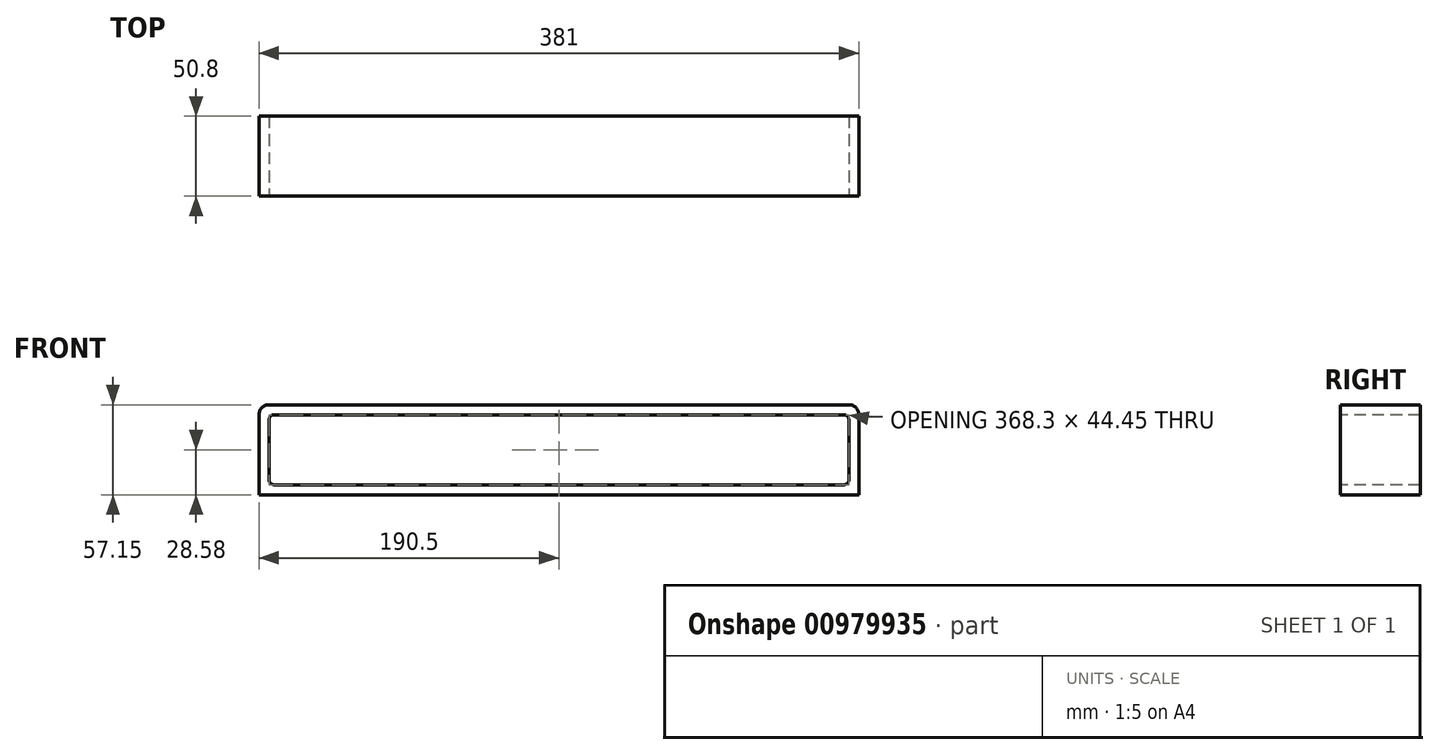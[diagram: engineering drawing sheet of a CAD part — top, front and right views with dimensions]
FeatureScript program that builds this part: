
annotation { "Feature Type Name" : "Feature", "Feature Type Description" : "" }
export const myFeature = defineFeature(function(context is Context, id is Id, definition is map)
    precondition{}
    {
        {
            var Q0;
            Q0=qCreatedBy(makeId("Front.planeOp"),FACE);
            var sketch = newSketch(context, id + "F0", { "sketchPlane" : qUnion([Q0])});
            skLineSegment(sketch, "E0.bottom", {"start": v(190.5, -28.57) * mm, "end": v(-190.5, -28.58) * mm});
            skLineSegment(sketch, "E0.top", {"start": v(190.5, 28.58) * mm, "end": v(-190.5, 28.57) * mm});
            skLineSegment(sketch, "E0.left", {"start": v(190.5, -28.57) * mm, "end": v(190.5, 28.58) * mm});
            skLineSegment(sketch, "E0.right", {"start": v(-190.5, -28.58) * mm, "end": v(-190.5, 28.57) * mm});
            skPoint(sketch, "E0.middle", {"position": v(0, 0) * mm});
            skSolve(sketch);
        }
        {
            var Q0;
            Q0=makeQuery(id+"F0.imprint","IMPRINT",FACE,{"disambiguationData":[TD([[makeQuery(id+"F0.imprint","IMPRINT",EDGE,{"derivedFrom":sQuery(id+"F0.wireOp",EDGE,"E0.bottom")}),-1.0]])]});
            extrude(context, id + "F1", {"entities" : qUnion([Q0]), "depth" : 50.8 * mm, "offsetDistance" : 25.4 * mm});
        }
        {
            var Q0;
            Q0=makeQuery(id+"F1.opExtrude","SWEPT_BODY",BODY,{"disambiguationData":[OSD([sQuery(id+"F0.wireOp",EDGE,"E0.bottom"),sQuery(id+"F0.wireOp",EDGE,"E0.top"),sQuery(id+"F0.wireOp",EDGE,"E0.left"),sQuery(id+"F0.wireOp",EDGE,"E0.right")])]});
            transform(context, id + "F2", {"entities" : qUnion([Q0]), "transformType" : TransformType.TRANSLATION_3D, "dx" : 0 * mm, "dy" : 50.8 * mm, "dz" : 0 * mm, "makeCopy" : false});
        }
        {
            var Q0;
            Q0=qCreatedBy(makeId("Front.planeOp"),FACE);
            var sketch = newSketch(context, id + "F3", { "sketchPlane" : qUnion([Q0])});
            skLineSegment(sketch, "E1.bottom", {"start": v(184.15, -22.22) * mm, "end": v(-184.15, -22.23) * mm});
            skLineSegment(sketch, "E1.top", {"start": v(184.15, 22.23) * mm, "end": v(-184.15, 22.22) * mm});
            skLineSegment(sketch, "E1.left", {"start": v(184.15, -22.22) * mm, "end": v(184.15, 22.23) * mm});
            skLineSegment(sketch, "E1.right", {"start": v(-184.15, -22.23) * mm, "end": v(-184.15, 22.22) * mm});
            skPoint(sketch, "E1.middle", {"position": v(0, 0) * mm});
            skSolve(sketch);
        }
        {
            var Q0;
            Q0=makeQuery(id+"F3.imprint","IMPRINT",FACE,{"disambiguationData":[TD([[makeQuery(id+"F3.imprint","IMPRINT",EDGE,{"derivedFrom":sQuery(id+"F3.wireOp",EDGE,"E1.bottom")}),-1.0]])]});
            extrude(context, id + "F4", {"entities" : qUnion([Q0]), "operationType" : NewBodyOperationType.REMOVE, "oppositeDirection" : true, "depth" : 50.8 * mm, "offsetDistance" : 25.4 * mm});
        }
        {
            var Q0;
            Q0=makeQuery(id+"F4.boolean.opBoolean","COPY",EDGE,{"derivedFrom":makeQuery(id+"F4.opExtrude","SWEPT_EDGE",EDGE,{"disambiguationData":[OSD([sQuery(id+"F3.wireOp",EDGE,"E1.bottom"),sQuery(id+"F3.wireOp",EDGE,"E1.left")])]})});
            var Q1;
            Q1=makeQuery(id+"F4.boolean.opBoolean","COPY",EDGE,{"derivedFrom":makeQuery(id+"F4.opExtrude","SWEPT_EDGE",EDGE,{"disambiguationData":[OSD([sQuery(id+"F3.wireOp",EDGE,"E1.top"),sQuery(id+"F3.wireOp",EDGE,"E1.left")])]})});
            var Q2;
            Q2=makeQuery(id+"F4.boolean.opBoolean","COPY",EDGE,{"derivedFrom":makeQuery(id+"F4.opExtrude","SWEPT_EDGE",EDGE,{"disambiguationData":[OSD([sQuery(id+"F3.wireOp",EDGE,"E1.top"),sQuery(id+"F3.wireOp",EDGE,"E1.right")])]})});
            var Q3;
            Q3=makeQuery(id+"F4.boolean.opBoolean","COPY",EDGE,{"derivedFrom":makeQuery(id+"F4.opExtrude","SWEPT_EDGE",EDGE,{"disambiguationData":[OSD([sQuery(id+"F3.wireOp",EDGE,"E1.bottom"),sQuery(id+"F3.wireOp",EDGE,"E1.right")])]})});
            fillet(context, id + "F5", {"entities" : qUnion([Q0, Q1, Q2, Q3]), "radius" : 3.17 * mm, "tangentPropagation" : true, "allowEdgeOverflow" : false});
        }
        {
            var Q0;
            Q0=makeQuery(id+"F1.opExtrude","SWEPT_BODY",BODY,{"disambiguationData":[OSD([sQuery(id+"F0.wireOp",EDGE,"E0.bottom"),sQuery(id+"F0.wireOp",EDGE,"E0.top"),sQuery(id+"F0.wireOp",EDGE,"E0.left"),sQuery(id+"F0.wireOp",EDGE,"E0.right")])]});
            transform(context, id + "F6", {"entities" : qUnion([Q0]), "transformType" : TransformType.TRANSLATION_3D, "dx" : 0 * mm, "dy" : 50.8 * mm, "dz" : 0 * mm, "makeCopy" : false});
        }
        {
            var Q0;
            Q0=makeQuery(id+"F1.opExtrude","SWEPT_BODY",BODY,{"disambiguationData":[OSD([sQuery(id+"F0.wireOp",EDGE,"E0.bottom"),sQuery(id+"F0.wireOp",EDGE,"E0.top"),sQuery(id+"F0.wireOp",EDGE,"E0.left"),sQuery(id+"F0.wireOp",EDGE,"E0.right")])]});
            transform(context, id + "F7", {"entities" : qUnion([Q0]), "transformType" : TransformType.TRANSLATION_3D, "dx" : 0 * mm, "dy" : 0 * mm, "dz" : -101.6 * mm, "makeCopy" : false});
        }
        {
            var Q0;
            Q0=makeQuery(id+"F1.opExtrude","SWEPT_BODY",BODY,{"disambiguationData":[OSD([sQuery(id+"F0.wireOp",EDGE,"E0.bottom"),sQuery(id+"F0.wireOp",EDGE,"E0.top"),sQuery(id+"F0.wireOp",EDGE,"E0.left"),sQuery(id+"F0.wireOp",EDGE,"E0.right")])]});
            transform(context, id + "F8", {"entities" : qUnion([Q0]), "transformType" : TransformType.TRANSLATION_3D, "dx" : 0 * mm, "dy" : 50.8 * mm, "dz" : 50.8 * mm, "makeCopy" : false});
        }
        {
            var Q0;
            Q0=makeQuery(id+"F1.opExtrude","SWEPT_EDGE",EDGE,{"disambiguationData":[OSD([sQuery(id+"F0.wireOp",EDGE,"E0.top"),sQuery(id+"F0.wireOp",EDGE,"E0.left")])]});
            var Q1;
            Q1=makeQuery(id+"F1.opExtrude","SWEPT_EDGE",EDGE,{"disambiguationData":[OSD([sQuery(id+"F0.wireOp",EDGE,"E0.top"),sQuery(id+"F0.wireOp",EDGE,"E0.right")])]});
            fillet(context, id + "F9", {"entities" : qUnion([Q0, Q1]), "radius" : 6.35 * mm, "tangentPropagation" : true, "allowEdgeOverflow" : false});
        }
    });
